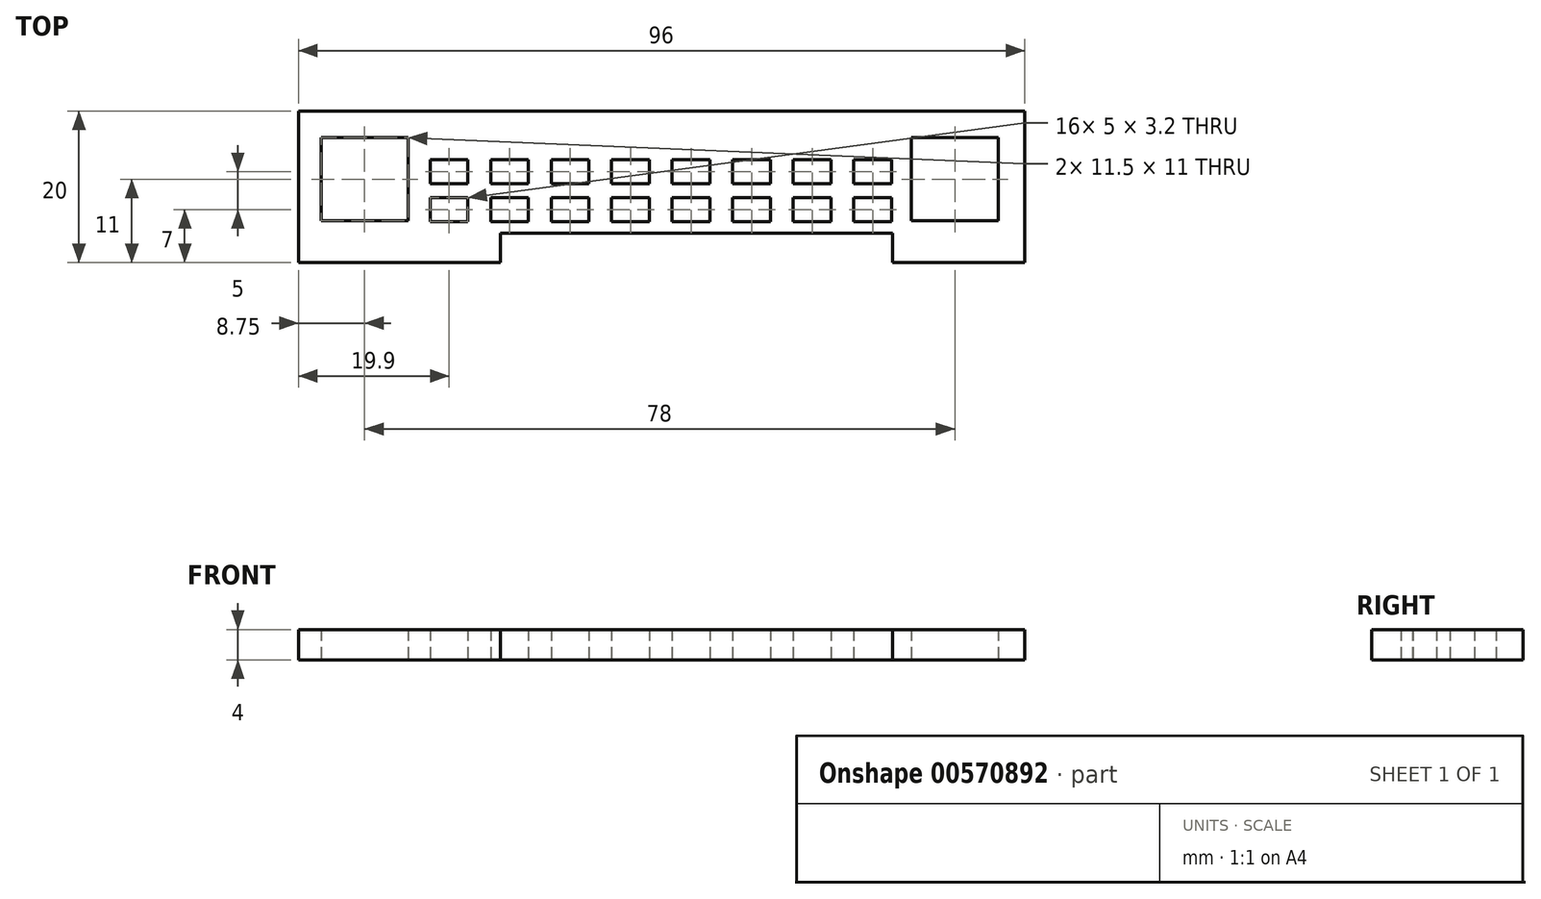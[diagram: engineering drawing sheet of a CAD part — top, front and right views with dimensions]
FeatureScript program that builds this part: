
annotation { "Feature Type Name" : "Feature", "Feature Type Description" : "" }
export const myFeature = defineFeature(function(context is Context, id is Id, definition is map)
    precondition{}
    {
        {
            var Q0;
            Q0=qCreatedBy(makeId("Top.planeOp"),FACE);
            var sketch = newSketch(context, id + "F0", { "sketchPlane" : qUnion([Q0])});
            skLineSegment(sketch, "E0.bottom", {"start": v(0, 0) * mm, "end": v(96, 0) * mm});
            skLineSegment(sketch, "E0.top", {"start": v(0, 20) * mm, "end": v(96, 20) * mm});
            skLineSegment(sketch, "E0.left", {"start": v(0, 0) * mm, "end": v(0, 20) * mm});
            skLineSegment(sketch, "E0.right", {"start": v(96, 0) * mm, "end": v(96, 20) * mm});
            skSolve(sketch);
        }
        {
            var Q0;
            Q0=qCreatedBy(makeId("Top.planeOp"),FACE);
            var sketch = newSketch(context, id + "F1", { "sketchPlane" : qUnion([Q0])});
            skLineSegment(sketch, "E1.bottom", {"start": v(3, 5.5) * mm, "end": v(14.5, 5.5) * mm});
            skLineSegment(sketch, "E1.top", {"start": v(3, 16.5) * mm, "end": v(14.5, 16.5) * mm});
            skLineSegment(sketch, "E1.left", {"start": v(3, 5.5) * mm, "end": v(3, 16.5) * mm});
            skLineSegment(sketch, "E1.right", {"start": v(14.5, 5.5) * mm, "end": v(14.5, 16.5) * mm});
            skLineSegment(sketch, "E2.bottom", {"start": v(92.5, 16.5) * mm, "end": v(81, 16.5) * mm});
            skLineSegment(sketch, "E2.top", {"start": v(92.5, 5.5) * mm, "end": v(81, 5.5) * mm});
            skLineSegment(sketch, "E2.left", {"start": v(92.5, 16.5) * mm, "end": v(92.5, 5.5) * mm});
            skLineSegment(sketch, "E2.right", {"start": v(81, 16.5) * mm, "end": v(81, 5.5) * mm});
            skLineSegment(sketch, "E3.bottom", {"start": v(22.4, 10.4) * mm, "end": v(17.4, 10.4) * mm});
            skLineSegment(sketch, "E3.top", {"start": v(22.4, 13.6) * mm, "end": v(17.4, 13.6) * mm});
            skLineSegment(sketch, "E3.left", {"start": v(22.4, 10.4) * mm, "end": v(22.4, 13.6) * mm});
            skLineSegment(sketch, "E3.right", {"start": v(17.4, 10.4) * mm, "end": v(17.4, 13.6) * mm});
            skPoint(sketch, "E3.middle", {"position": v(19.9, 12) * mm});
            skLineSegment(sketch, "E4.0.1.0", {"start": v(22.4, 5.4) * mm, "end": v(17.4, 5.4) * mm});
            skLineSegment(sketch, "E4.0.1.1", {"start": v(22.4, 5.4) * mm, "end": v(22.4, 8.6) * mm});
            skLineSegment(sketch, "E4.0.1.2", {"start": v(22.4, 8.6) * mm, "end": v(17.4, 8.6) * mm});
            skLineSegment(sketch, "E4.0.1.3", {"start": v(17.4, 5.4) * mm, "end": v(17.4, 8.6) * mm});
            skLineSegment(sketch, "E4.1.0.0", {"start": v(30.4, 10.4) * mm, "end": v(25.4, 10.4) * mm});
            skLineSegment(sketch, "E4.1.0.1", {"start": v(30.4, 10.4) * mm, "end": v(30.4, 13.6) * mm});
            skLineSegment(sketch, "E4.1.0.2", {"start": v(30.4, 13.6) * mm, "end": v(25.4, 13.6) * mm});
            skLineSegment(sketch, "E4.1.0.3", {"start": v(25.4, 10.4) * mm, "end": v(25.4, 13.6) * mm});
            skLineSegment(sketch, "E4.1.1.0", {"start": v(30.4, 5.4) * mm, "end": v(25.4, 5.4) * mm});
            skLineSegment(sketch, "E4.1.1.1", {"start": v(30.4, 5.4) * mm, "end": v(30.4, 8.6) * mm});
            skLineSegment(sketch, "E4.1.1.2", {"start": v(30.4, 8.6) * mm, "end": v(25.4, 8.6) * mm});
            skLineSegment(sketch, "E4.1.1.3", {"start": v(25.4, 5.4) * mm, "end": v(25.4, 8.6) * mm});
            skLineSegment(sketch, "E4.2.0.0", {"start": v(38.4, 10.4) * mm, "end": v(33.4, 10.4) * mm});
            skLineSegment(sketch, "E4.2.0.1", {"start": v(38.4, 10.4) * mm, "end": v(38.4, 13.6) * mm});
            skLineSegment(sketch, "E4.2.0.2", {"start": v(38.4, 13.6) * mm, "end": v(33.4, 13.6) * mm});
            skLineSegment(sketch, "E4.2.0.3", {"start": v(33.4, 10.4) * mm, "end": v(33.4, 13.6) * mm});
            skLineSegment(sketch, "E4.2.1.0", {"start": v(38.4, 5.4) * mm, "end": v(33.4, 5.4) * mm});
            skLineSegment(sketch, "E4.2.1.1", {"start": v(38.4, 5.4) * mm, "end": v(38.4, 8.6) * mm});
            skLineSegment(sketch, "E4.2.1.2", {"start": v(38.4, 8.6) * mm, "end": v(33.4, 8.6) * mm});
            skLineSegment(sketch, "E4.2.1.3", {"start": v(33.4, 5.4) * mm, "end": v(33.4, 8.6) * mm});
            skLineSegment(sketch, "E4.3.0.0", {"start": v(46.4, 10.4) * mm, "end": v(41.4, 10.4) * mm});
            skLineSegment(sketch, "E4.3.0.1", {"start": v(46.4, 10.4) * mm, "end": v(46.4, 13.6) * mm});
            skLineSegment(sketch, "E4.3.0.2", {"start": v(46.4, 13.6) * mm, "end": v(41.4, 13.6) * mm});
            skLineSegment(sketch, "E4.3.0.3", {"start": v(41.4, 10.4) * mm, "end": v(41.4, 13.6) * mm});
            skLineSegment(sketch, "E4.3.1.0", {"start": v(46.4, 5.4) * mm, "end": v(41.4, 5.4) * mm});
            skLineSegment(sketch, "E4.3.1.1", {"start": v(46.4, 5.4) * mm, "end": v(46.4, 8.6) * mm});
            skLineSegment(sketch, "E4.3.1.2", {"start": v(46.4, 8.6) * mm, "end": v(41.4, 8.6) * mm});
            skLineSegment(sketch, "E4.3.1.3", {"start": v(41.4, 5.4) * mm, "end": v(41.4, 8.6) * mm});
            skLineSegment(sketch, "E4.4.0.0", {"start": v(54.4, 10.4) * mm, "end": v(49.4, 10.4) * mm});
            skLineSegment(sketch, "E4.4.0.1", {"start": v(54.4, 10.4) * mm, "end": v(54.4, 13.6) * mm});
            skLineSegment(sketch, "E4.4.0.2", {"start": v(54.4, 13.6) * mm, "end": v(49.4, 13.6) * mm});
            skLineSegment(sketch, "E4.4.0.3", {"start": v(49.4, 10.4) * mm, "end": v(49.4, 13.6) * mm});
            skLineSegment(sketch, "E4.4.1.0", {"start": v(54.4, 5.4) * mm, "end": v(49.4, 5.4) * mm});
            skLineSegment(sketch, "E4.4.1.1", {"start": v(54.4, 5.4) * mm, "end": v(54.4, 8.6) * mm});
            skLineSegment(sketch, "E4.4.1.2", {"start": v(54.4, 8.6) * mm, "end": v(49.4, 8.6) * mm});
            skLineSegment(sketch, "E4.4.1.3", {"start": v(49.4, 5.4) * mm, "end": v(49.4, 8.6) * mm});
            skLineSegment(sketch, "E4.5.0.0", {"start": v(62.4, 10.4) * mm, "end": v(57.4, 10.4) * mm});
            skLineSegment(sketch, "E4.5.0.1", {"start": v(62.4, 10.4) * mm, "end": v(62.4, 13.6) * mm});
            skLineSegment(sketch, "E4.5.0.2", {"start": v(62.4, 13.6) * mm, "end": v(57.4, 13.6) * mm});
            skLineSegment(sketch, "E4.5.0.3", {"start": v(57.4, 10.4) * mm, "end": v(57.4, 13.6) * mm});
            skLineSegment(sketch, "E4.5.1.0", {"start": v(62.4, 5.4) * mm, "end": v(57.4, 5.4) * mm});
            skLineSegment(sketch, "E4.5.1.1", {"start": v(62.4, 5.4) * mm, "end": v(62.4, 8.6) * mm});
            skLineSegment(sketch, "E4.5.1.2", {"start": v(62.4, 8.6) * mm, "end": v(57.4, 8.6) * mm});
            skLineSegment(sketch, "E4.5.1.3", {"start": v(57.4, 5.4) * mm, "end": v(57.4, 8.6) * mm});
            skLineSegment(sketch, "E4.6.0.0", {"start": v(70.4, 10.4) * mm, "end": v(65.4, 10.4) * mm});
            skLineSegment(sketch, "E4.6.0.1", {"start": v(70.4, 10.4) * mm, "end": v(70.4, 13.6) * mm});
            skLineSegment(sketch, "E4.6.0.2", {"start": v(70.4, 13.6) * mm, "end": v(65.4, 13.6) * mm});
            skLineSegment(sketch, "E4.6.0.3", {"start": v(65.4, 10.4) * mm, "end": v(65.4, 13.6) * mm});
            skLineSegment(sketch, "E4.6.1.0", {"start": v(70.4, 5.4) * mm, "end": v(65.4, 5.4) * mm});
            skLineSegment(sketch, "E4.6.1.1", {"start": v(70.4, 5.4) * mm, "end": v(70.4, 8.6) * mm});
            skLineSegment(sketch, "E4.6.1.2", {"start": v(70.4, 8.6) * mm, "end": v(65.4, 8.6) * mm});
            skLineSegment(sketch, "E4.6.1.3", {"start": v(65.4, 5.4) * mm, "end": v(65.4, 8.6) * mm});
            skLineSegment(sketch, "E4.7.0.0", {"start": v(78.4, 10.4) * mm, "end": v(73.4, 10.4) * mm});
            skLineSegment(sketch, "E4.7.0.1", {"start": v(78.4, 10.4) * mm, "end": v(78.4, 13.6) * mm});
            skLineSegment(sketch, "E4.7.0.2", {"start": v(78.4, 13.6) * mm, "end": v(73.4, 13.6) * mm});
            skLineSegment(sketch, "E4.7.0.3", {"start": v(73.4, 10.4) * mm, "end": v(73.4, 13.6) * mm});
            skLineSegment(sketch, "E4.7.1.0", {"start": v(78.4, 5.4) * mm, "end": v(73.4, 5.4) * mm});
            skLineSegment(sketch, "E4.7.1.1", {"start": v(78.4, 5.4) * mm, "end": v(78.4, 8.6) * mm});
            skLineSegment(sketch, "E4.7.1.2", {"start": v(78.4, 8.6) * mm, "end": v(73.4, 8.6) * mm});
            skLineSegment(sketch, "E4.7.1.3", {"start": v(73.4, 5.4) * mm, "end": v(73.4, 8.6) * mm});
            skLineSegment(sketch, "E4.direction1", {"start": v(17.4, 10.4) * mm, "end": v(25.4, 10.4) * mm, "construction": true});
            skLineSegment(sketch, "E4.direction2", {"start": v(17.4, 10.4) * mm, "end": v(17.4, 5.4) * mm, "construction": true});
            skLineSegment(sketch, "E5.bottom", {"start": v(26.7, 0) * mm, "end": v(78.5, 0) * mm});
            skLineSegment(sketch, "E5.top", {"start": v(26.7, 3.9) * mm, "end": v(78.5, 3.9) * mm});
            skLineSegment(sketch, "E5.left", {"start": v(26.7, 0) * mm, "end": v(26.7, 3.9) * mm});
            skLineSegment(sketch, "E5.right", {"start": v(78.5, 0) * mm, "end": v(78.5, 3.9) * mm});
            skSolve(sketch);
        }
        {
            var Q0;
            Q0=makeQuery(id+"F0.imprint","IMPRINT",FACE,{"disambiguationData":[TD([[makeQuery(id+"F0.imprint","IMPRINT",EDGE,{"derivedFrom":sQuery(id+"F0.wireOp",EDGE,"E0.bottom")}),1.0]])]});
            extrude(context, id + "F2", {"entities" : qUnion([Q0]), "depth" : 4 * mm, "offsetDistance" : 25 * mm});
        }
        {
            var Q0;
            Q0 = qSketchRegion(id + "F1", true);
            extrude(context, id + "F3", {"entities" : qUnion([Q0]), "operationType" : NewBodyOperationType.REMOVE, "endBound" : BoundingType.THROUGH_ALL, "depth" : 25 * mm, "offsetDistance" : 25 * mm});
        }
    });
